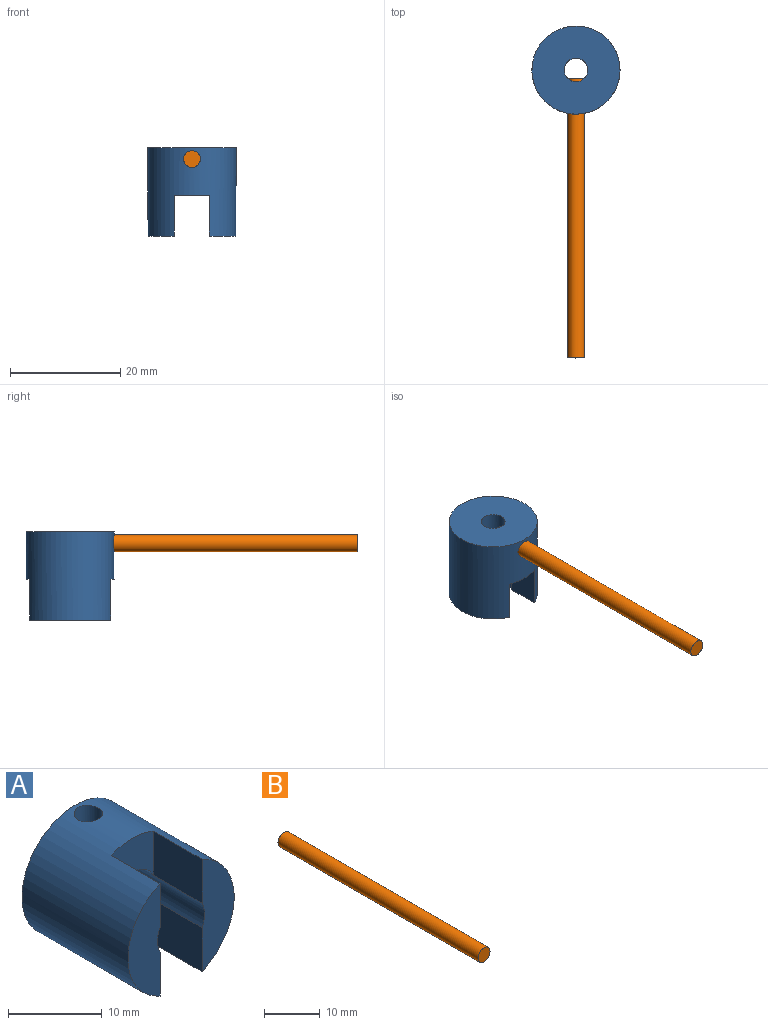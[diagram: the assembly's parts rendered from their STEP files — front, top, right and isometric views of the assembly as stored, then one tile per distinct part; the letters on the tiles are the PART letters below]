
ASSEMBLY  parts=2 mates=1
PART A: 14 faces, bbox 16x16x16 mm
  f0: plane 7.37x5.74mm, normal (1,0,0), area 42.3mm2, adj f5,f6,f10,f11
  f1: plane 7.37x5.74mm, normal (-1,0,0), area 42.3mm2, adj f4,f5,f10,f11
  f2: plane 6.4x6.35mm, normal (0,-1,0), area 30.4mm2, adj f5,f8,f9,f11
  f3: cylinder r=2.16mm len=4.83mm, axis (0,1,0), area 57.6mm2, adj f7,f12,f13
  f4: plane 14.69x4.83mm, normal (0,-1,0), area 50.3mm2, adj f1,f5,f9,f11
  f5: cylinder r=8mm len=16mm, axis (0,1,0), area 700.9mm2, adj f0,f1,f2,f4,f6,f7,f8,f9
  f6: plane 14.69x4.83mm, normal (0,-1,0), area 50.3mm2, adj f0,f5,f8,f11
  f7: plane 16x16mm, normal (0,1,0), area 186.5mm2, adj f3,f5
  f8: plane 7.37x5.74mm, normal (1,0,0), area 42.3mm2, adj f2,f5,f6,f11
  f9: plane 7.37x5.74mm, normal (-1,0,0), area 42.3mm2, adj f2,f4,f5,f11
  f10: plane 6.4x6.35mm, normal (0,-1,0), area 30.4mm2, adj f0,f1,f5,f11
  f11: cylinder r=3.56mm len=11.18mm, axis (0,-1,0), area 134.1mm2, adj f0,f1,f2,f4,f6,f8,f9,f10
  f12: plane 7.11x7.11mm, normal (0,-1,0), area 25.1mm2, adj f3,f11
  f13: cylinder r=1.52mm len=6.47mm, axis (0,0,1), area 58.1mm2, adj f3,f5
PART B: 3 faces, bbox 3x50.8x3 mm
  f0: cylinder r=1.52mm len=50.8mm, axis (0,1,0), area 486.4mm2, adj f1,f2
  f1: plane 3.05x3.05mm, normal (0,-1,0), area 7.3mm2, adj f0
  f2: plane 3.05x3.05mm, normal (0,1,0), area 7.3mm2, adj f0
PLACE A rot(axis=(1,0,0),90deg) t=(-6.1,4.43,11.75)mm
PLACE B t=(-6.1,2.94,9.72)mm
MATE parallel B.f0 <-> A.f13  axis (0,1,0) through (-6.1,2.94,9.72)mm
